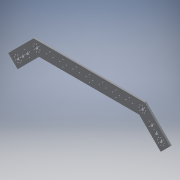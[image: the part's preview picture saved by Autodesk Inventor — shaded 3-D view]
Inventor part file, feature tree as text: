
AUTODESK INVENTOR PART (.ipt)
format: ipt  version: 2016 (Build 200138000, 138)  size: 195,584 bytes
history: native  units: mm
features: reference x10, extrude x1, sketch x1
ambient origin geometry x8: Origin, YZ Plane, XZ Plane, XY Plane, X Axis, Y Axis, Z Axis, Center Point
bodies: Body1 (feature_tree)
feature tree (12):
  extrude  "Extrusion2"  [1 undecoded]
  sketch  "Sketch1"  dims[d2=4.0mm d3=0.0mm]
  reference  "Reference2"
  reference  "Reference3"
  reference  "Reference4"
  reference  "Reference5"
  reference  "Reference6"
  reference  "Reference7"
  reference  "Reference8"
  reference  "Reference9"
  reference  "Reference10"
  reference  "Reference11"
note: 1 required parameter value undecoded (feature->parameter linkage not recoverable at this tier; creation-order binding heuristic only, values carry confidence <= 0.55)
